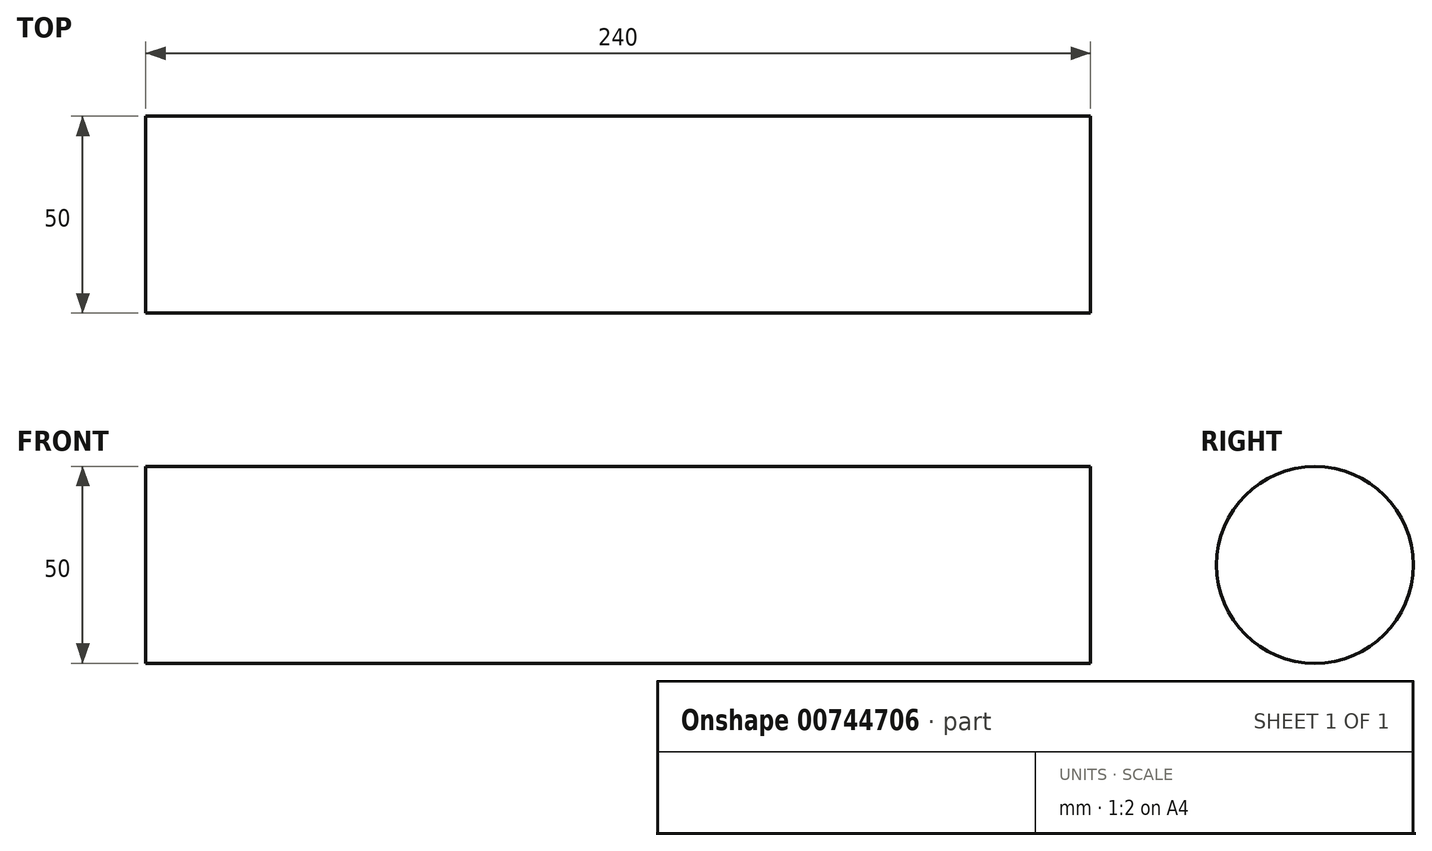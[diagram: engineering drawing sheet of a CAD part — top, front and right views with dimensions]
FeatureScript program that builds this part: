
annotation { "Feature Type Name" : "Feature", "Feature Type Description" : "" }
export const myFeature = defineFeature(function(context is Context, id is Id, definition is map)
    precondition{}
    {
        {
            var Q0;
            Q0=qCreatedBy(makeId("Top.planeOp"),FACE);
            var sketch = newSketch(context, id + "F0", { "sketchPlane" : qUnion([Q0])});
            skLineSegment(sketch, "E0", {"start": v(0, 0) * mm, "end": v(240, 0) * mm});
            skLineSegment(sketch, "E1.bottom", {"start": v(0, 25) * mm, "end": v(240, 25) * mm});
            skLineSegment(sketch, "E1.top", {"start": v(0, -25) * mm, "end": v(240, -25) * mm});
            skLineSegment(sketch, "E1.left", {"start": v(0, 25) * mm, "end": v(0, -25) * mm});
            skLineSegment(sketch, "E1.right", {"start": v(240, 25) * mm, "end": v(240, -25) * mm});
            skSolve(sketch);
        }
        {
            var Q0;
            Q0=makeQuery(id+"F0.imprint","IMPRINT",FACE,{"disambiguationData":[TD([[makeQuery(id+"F0.imprint","IMPRINT",EDGE,{"derivedFrom":sQuery(id+"F0.wireOp",EDGE,"E1.bottom")}),-1.0]])]});
            var Q1;
            Q1=sQuery(id+"F0.wireOp",EDGE,"E0");
            revolve(context, id + "F1", {"surfaceOperationType" : NewSurfaceOperationType.NEW, "entities" : qUnion([Q0]), "axis" : qUnion([Q1]), "revolveType" : RevolveType.FULL});
        }
    });
